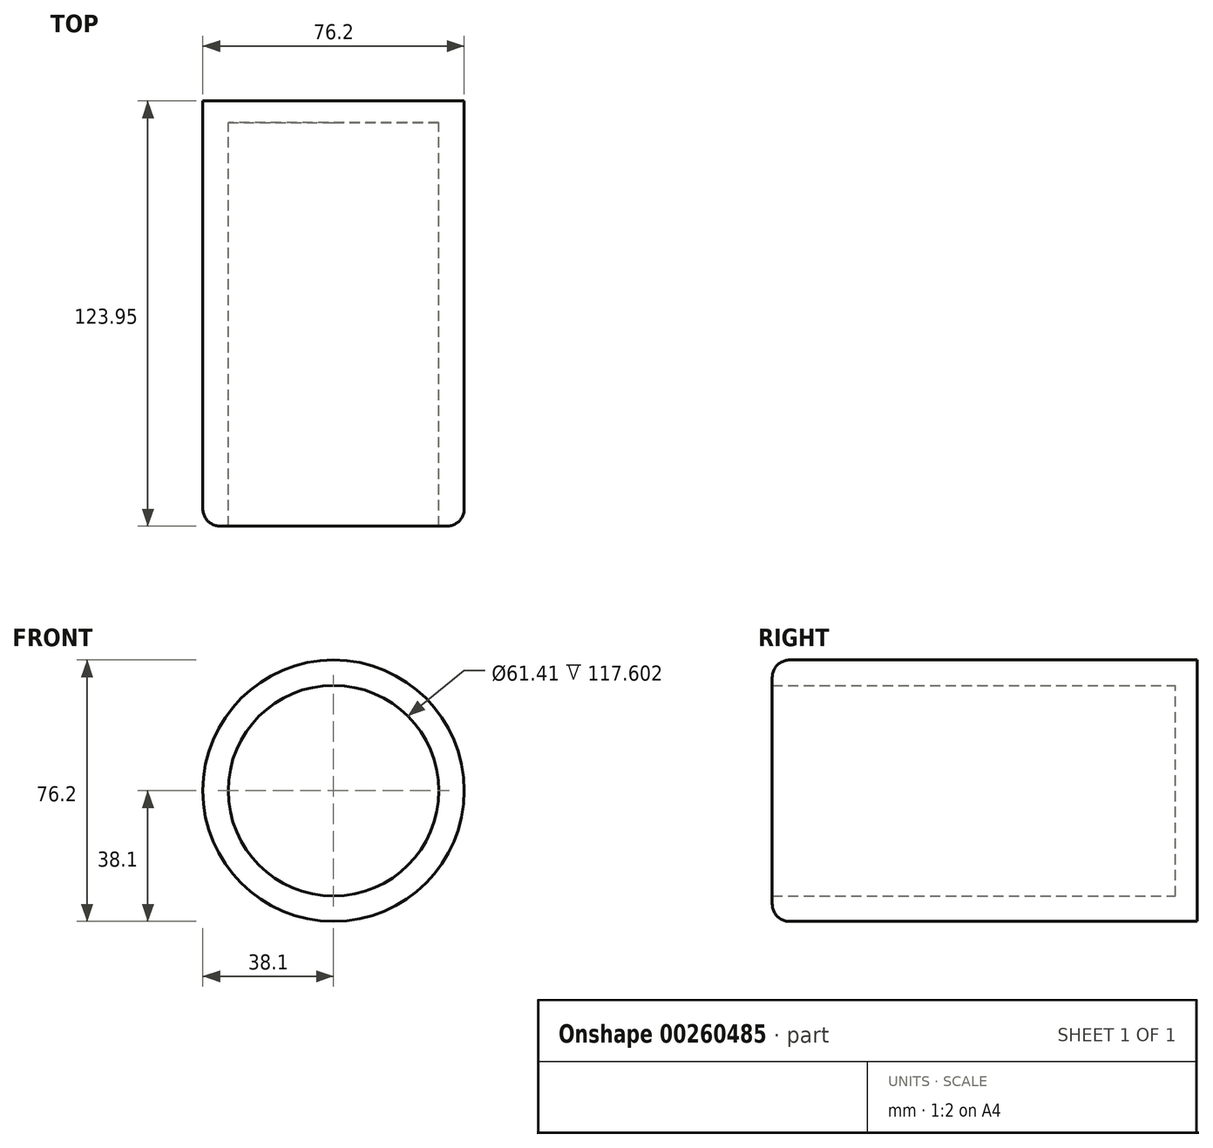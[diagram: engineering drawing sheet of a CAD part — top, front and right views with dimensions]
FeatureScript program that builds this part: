
annotation { "Feature Type Name" : "Feature", "Feature Type Description" : "" }
export const myFeature = defineFeature(function(context is Context, id is Id, definition is map)
    precondition{}
    {
        {
            var Q0;
            Q0=qCreatedBy(makeId("Front.planeOp"),FACE);
            var sketch = newSketch(context, id + "F0", { "sketchPlane" : qUnion([Q0])});
            skCircle(sketch, "E0", {"center": v(0, 0) * mm, "radius": 38.1 * mm});
            skCircle(sketch, "E1", {"center": v(0, 0) * mm, "radius": 30.7 * mm});
            skSolve(sketch);
        }
        {
            var Q0;
            Q0=makeQuery(id+"F0.imprint","IMPRINT",FACE,{"disambiguationData":[TD([[makeQuery(id+"F0.imprint","IMPRINT",EDGE,{"derivedFrom":sQuery(id+"F0.wireOp",EDGE,"E0")}),1.0]])]});
            extrude(context, id + "F1", {"entities" : qUnion([Q0]), "depth" : 123.95 * mm});
        }
        {
            var Q0;
            Q0=makeQuery(id+"F1.opExtrude","CAP_EDGE",EDGE,{"disambiguationData":[OSD([sQuery(id+"F0.wireOp",EDGE,"E0")])],"isStart":false});
            fillet(context, id + "F2", {"entities" : qUnion([Q0]), "radius" : 5.08 * mm, "tangentPropagation" : true, "allowEdgeOverflow" : false});
        }
        {
            var Q0;
            Q0=qCreatedBy(makeId("Front.planeOp"),FACE);
            var sketch = newSketch(context, id + "F3", { "sketchPlane" : qUnion([Q0])});
            skCircle(sketch, "E2", {"center": v(0, 0) * mm, "radius": 30.74 * mm});
            skSolve(sketch);
        }
        {
            var Q0;
            Q0 = qSketchRegion(id + "F3", true);
            extrude(context, id + "F4", {"entities" : qUnion([Q0]), "operationType" : NewBodyOperationType.ADD, "depth" : 6.35 * mm});
        }
    });
